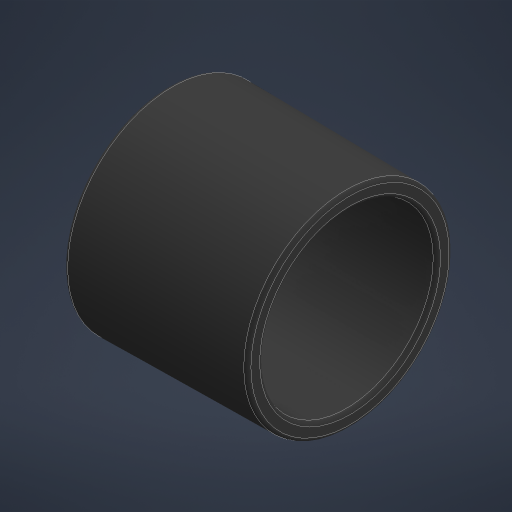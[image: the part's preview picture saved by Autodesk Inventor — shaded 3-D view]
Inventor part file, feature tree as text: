
AUTODESK INVENTOR PART (.ipt)
format: ipt  version: 2025 (Build 290162010, 162A)  size: 214,528 bytes
history: native  units: mm
features: revolve x1, sketch x1
ambient origin geometry x8: Origin, YZ Plane, XZ Plane, XY Plane, X Axis, Y Axis, Z Axis, Center Point
bodies: Solid1 (feature_tree)
feature tree (2):
  revolve  "Revolution1"  [1 undecoded]
  sketch  "Sketch1"  dims[d0=13.0mm d1=11.0mm d2=6.0mm d3=1.1mm d5=2.0mm d6=7.25mm d7=60.0mm d8=0.5mm d9=0.25mm d10=90.0deg d11=0.872665mm]
note: 1 required parameter value undecoded (feature->parameter linkage not recoverable at this tier; creation-order binding heuristic only, values carry confidence <= 0.55)
